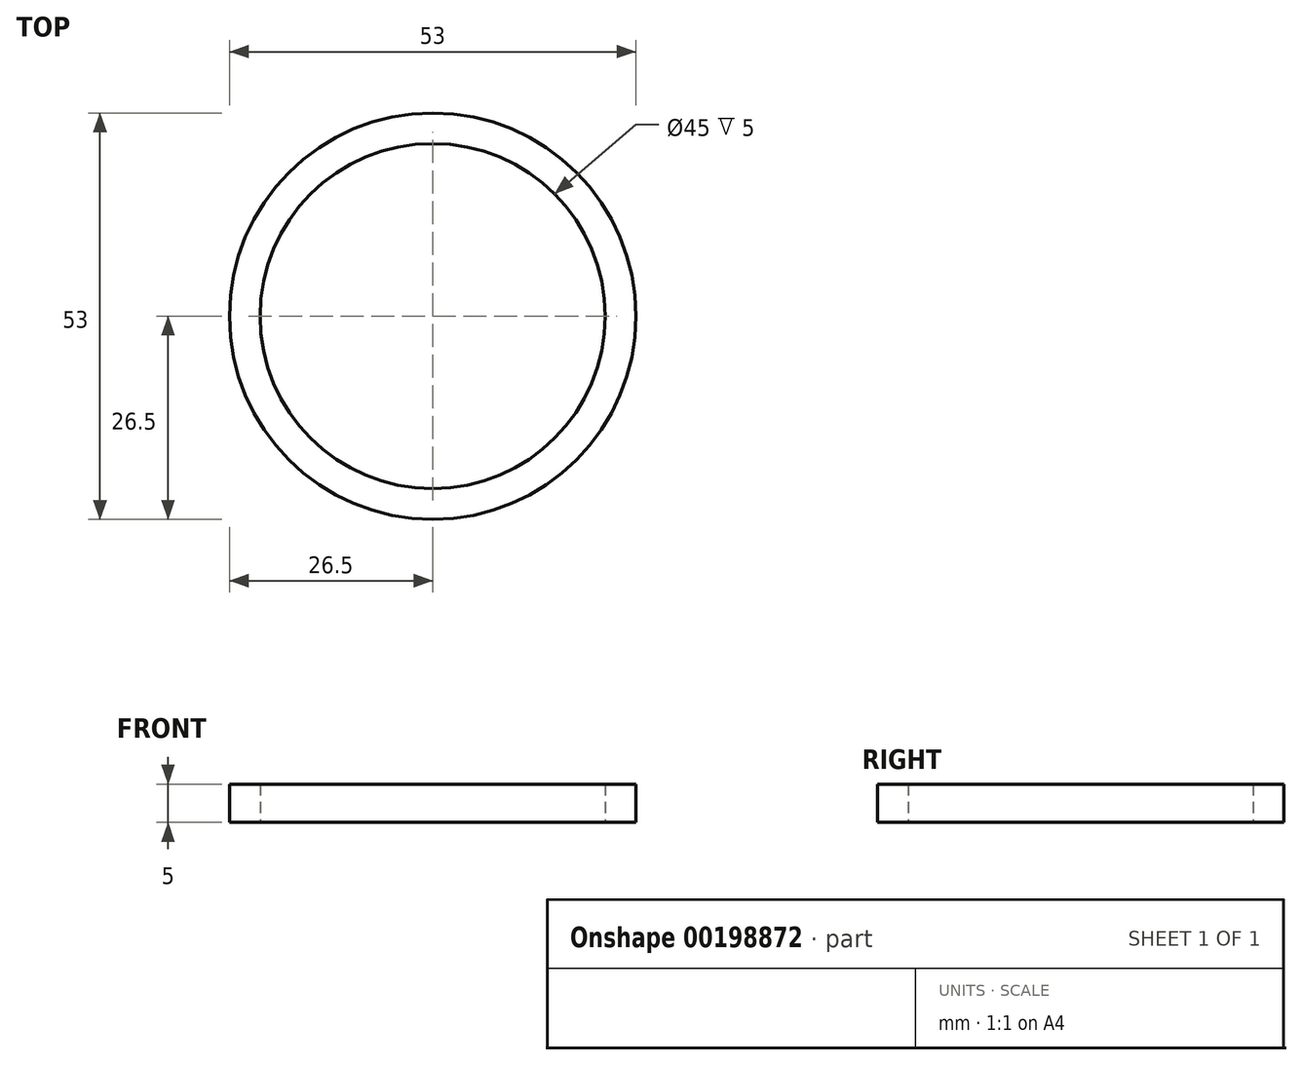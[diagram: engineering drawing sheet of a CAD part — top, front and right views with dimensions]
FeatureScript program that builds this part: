
annotation { "Feature Type Name" : "Feature", "Feature Type Description" : "" }
export const myFeature = defineFeature(function(context is Context, id is Id, definition is map)
    precondition{}
    {
        {
            var Q0;
            Q0=qCreatedBy(makeId("Top.planeOp"),FACE);
            var sketch = newSketch(context, id + "F0", { "sketchPlane" : qUnion([Q0])});
            skCircle(sketch, "E0", {"center": v(0, 0) * mm, "radius": 22.5 * mm});
            skCircle(sketch, "E1", {"center": v(0, 0) * mm, "radius": 26.5 * mm});
            skSolve(sketch);
        }
        {
            var Q0;
            Q0=makeQuery(id+"F0.imprint","IMPRINT",FACE,{"disambiguationData":[TD([[makeQuery(id+"F0.imprint","IMPRINT",EDGE,{"derivedFrom":sQuery(id+"F0.wireOp",EDGE,"E0")}),-1.0]])]});
            extrude(context, id + "F1", {"entities" : qUnion([Q0]), "depth" : 5 * mm});
        }
    });
